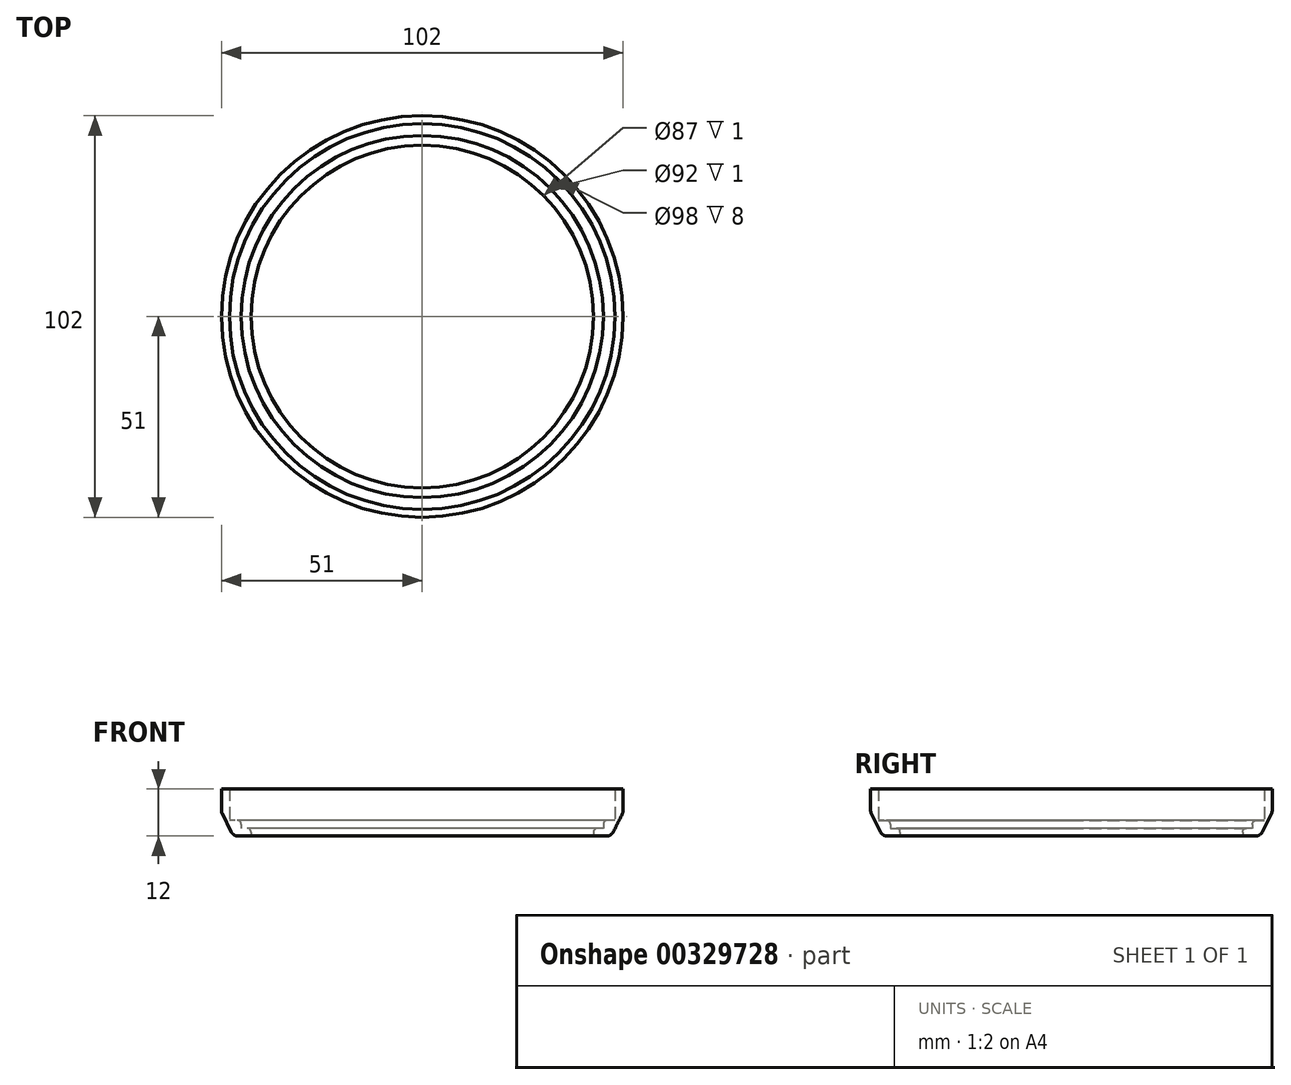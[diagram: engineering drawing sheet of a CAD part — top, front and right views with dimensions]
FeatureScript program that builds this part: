
annotation { "Feature Type Name" : "Feature", "Feature Type Description" : "" }
export const myFeature = defineFeature(function(context is Context, id is Id, definition is map)
    precondition{}
    {
        {
            var Q0;
            Q0=qCreatedBy(makeId("Top.planeOp"),FACE);
            var sketch = newSketch(context, id + "F0", { "sketchPlane" : qUnion([Q0])});
            skCircle(sketch, "E0", {"center": v(0, 0) * mm, "radius": 43.5 * mm});
            skCircle(sketch, "E1", {"center": v(0, 0) * mm, "radius": 46 * mm});
            skCircle(sketch, "E2", {"center": v(0, 0) * mm, "radius": 49 * mm});
            skCircle(sketch, "E3", {"center": v(0, 0) * mm, "radius": 51 * mm});
            skSolve(sketch);
        }
        {
            var Q0;
            Q0=makeQuery(id+"F0.imprint","IMPRINT",FACE,{"disambiguationData":[TD([[makeQuery(id+"F0.imprint","IMPRINT",EDGE,{"derivedFrom":sQuery(id+"F0.wireOp",EDGE,"E0")}),-1.0]])]});
            extrude(context, id + "F1", {"entities" : qUnion([Q0]), "depth" : 2 * mm});
        }
        {
            var Q0;
            Q0=makeQuery(id+"F0.imprint","IMPRINT",FACE,{"disambiguationData":[TD([[makeQuery(id+"F0.imprint","IMPRINT",EDGE,{"derivedFrom":sQuery(id+"F0.wireOp",EDGE,"E1")}),-1.0]])]});
            extrude(context, id + "F2", {"entities" : qUnion([Q0]), "operationType" : NewBodyOperationType.ADD, "depth" : 4 * mm});
        }
        {
            var Q0;
            Q0=makeQuery(id+"F0.imprint","IMPRINT",FACE,{"disambiguationData":[TD([[makeQuery(id+"F0.imprint","IMPRINT",EDGE,{"derivedFrom":sQuery(id+"F0.wireOp",EDGE,"E2")}),-1.0]])]});
            extrude(context, id + "F3", {"entities" : qUnion([Q0]), "operationType" : NewBodyOperationType.ADD, "depth" : 12 * mm});
        }
        {
            var Q0;
            Q0=makeQuery(id+"F1.opExtrude","CAP_EDGE",EDGE,{"disambiguationData":[OSD([sQuery(id+"F0.wireOp",EDGE,"E0")])],"isStart":false});
            var Q1;
            Q1=makeQuery(id+"F2.opExtrude","CAP_EDGE",EDGE,{"disambiguationData":[OSD([sQuery(id+"F0.wireOp",EDGE,"E1")])],"isStart":false});
            fillet(context, id + "F4", {"entities" : qUnion([Q0, Q1]), "radius" : 1 * mm, "tangentPropagation" : true, "allowEdgeOverflow" : false});
        }
        {
            var Q0;
            Q0=makeQuery(id+"F3.opExtrude","CAP_EDGE",EDGE,{"disambiguationData":[OSD([sQuery(id+"F0.wireOp",EDGE,"E3")])],"isStart":true});
            chamfer(context, id + "F5", {"entities" : qUnion([Q0]), "chamferType" : ChamferType.TWO_OFFSETS, "width1" : 6 * mm, "oppositeDirection" : false, "width2" : 3 * mm, "tangentPropagation" : true});
        }
        {
            var Q0;
            {var subQ0=sQuery(id+"F0.wireOp",EDGE,"E3");Q0=makeQuery(id+"F5.opChamfer","BLEND_EDGE",EDGE,{"blendedFrom":[makeQuery(id+"F3.opExtrude","CAP_EDGE",EDGE,{"disambiguationData":[OSD([subQ0])],"isStart":true}),makeQuery(id+"F3.opExtrude","SWEPT_FACE",FACE,{"disambiguationData":[OSD([subQ0])]})],"blendedInto":[makeQuery(id+"F3.opExtrude","SWEPT_FACE",FACE,{"disambiguationData":[OSD([subQ0])]})]});}
            var Q1;
            Q1=makeQuery(id+"F5.opChamfer","BLEND_FACE",FACE,{"disambiguationData":[OSD([sQuery(id+"F0.wireOp",EDGE,"E3")])]});
            fillet(context, id + "F6", {"entities" : qUnion([Q0, Q1]), "radius" : 2 * mm, "tangentPropagation" : true, "allowEdgeOverflow" : false});
        }
    });
